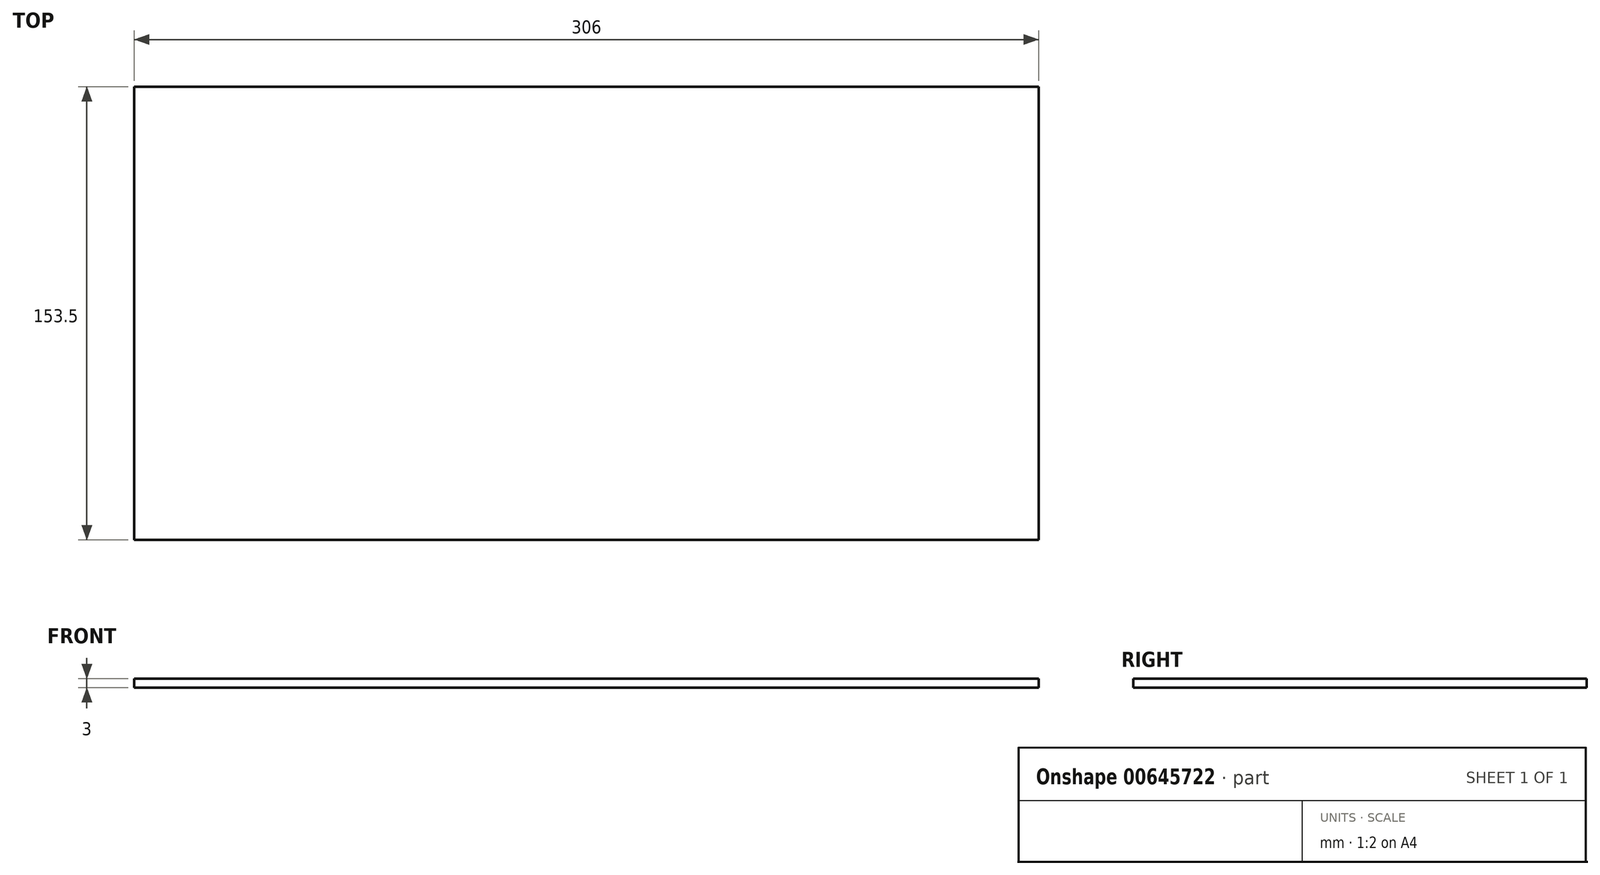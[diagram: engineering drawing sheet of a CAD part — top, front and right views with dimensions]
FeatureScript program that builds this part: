
annotation { "Feature Type Name" : "Feature", "Feature Type Description" : "" }
export const myFeature = defineFeature(function(context is Context, id is Id, definition is map)
    precondition{}
    {
        {
            var Q0;
            Q0=qCreatedBy(makeId("Top.planeOp"),FACE);
            var sketch = newSketch(context, id + "F0", { "sketchPlane" : qUnion([Q0])});
            skLineSegment(sketch, "E0.bottom", {"start": v(-153, 76.75) * mm, "end": v(153, 76.75) * mm});
            skLineSegment(sketch, "E0.top", {"start": v(-153, -76.75) * mm, "end": v(153, -76.75) * mm});
            skLineSegment(sketch, "E0.left", {"start": v(-153, 76.75) * mm, "end": v(-153, -76.75) * mm});
            skLineSegment(sketch, "E0.right", {"start": v(153, 76.75) * mm, "end": v(153, -76.75) * mm});
            skPoint(sketch, "E0.middle", {"position": v(0, 0) * mm});
            skSolve(sketch);
        }
        {
            var Q0;
            Q0=makeQuery(id+"F0.imprint","IMPRINT",FACE,{"disambiguationData":[TD([[makeQuery(id+"F0.imprint","IMPRINT",EDGE,{"derivedFrom":sQuery(id+"F0.wireOp",EDGE,"E0.bottom")}),-1.0]])]});
            extrude(context, id + "F1", {"entities" : qUnion([Q0]), "depth" : 3 * mm, "offsetDistance" : 25 * mm});
        }
    });
